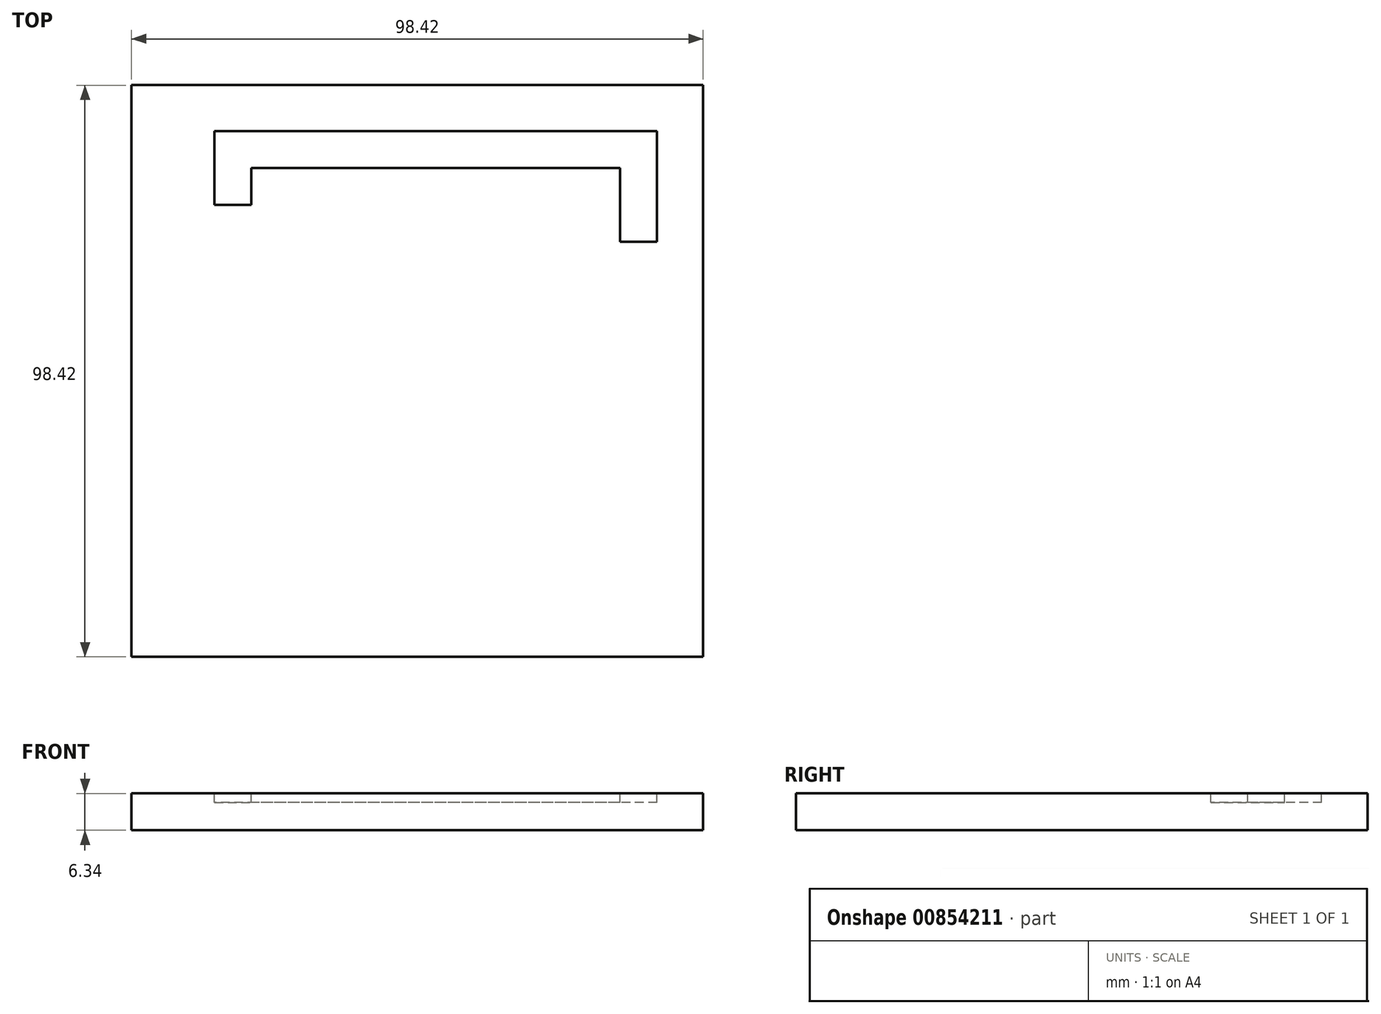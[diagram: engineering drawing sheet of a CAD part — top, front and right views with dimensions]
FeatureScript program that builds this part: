
annotation { "Feature Type Name" : "Feature", "Feature Type Description" : "" }
export const myFeature = defineFeature(function(context is Context, id is Id, definition is map)
    precondition{}
    {
        {
            var Q0;
            Q0=qCreatedBy(makeId("Top.planeOp"),FACE);
            var sketch = newSketch(context, id + "F0", { "sketchPlane" : qUnion([Q0])});
            skLineSegment(sketch, "E0.bottom", {"start": v(49.21, -49.21) * mm, "end": v(-49.21, -49.21) * mm});
            skLineSegment(sketch, "E0.top", {"start": v(49.21, 49.21) * mm, "end": v(-49.21, 49.21) * mm});
            skLineSegment(sketch, "E0.left", {"start": v(49.21, -49.21) * mm, "end": v(49.21, 49.21) * mm});
            skLineSegment(sketch, "E0.right", {"start": v(-49.21, -49.21) * mm, "end": v(-49.21, 49.21) * mm});
            skPoint(sketch, "E0.middle", {"position": v(0, 0) * mm});
            skSolve(sketch);
        }
        {
            var Q0;
            Q0 = qSketchRegion(id + "F0", true);
            extrude(context, id + "F1", {"entities" : qUnion([Q0]), "endBound" : BoundingType.SYMMETRIC, "depth" : 6.35 * mm, "offsetDistance" : 25.4 * mm});
        }
        {
            var Q0;
            Q0=makeQuery(id+"F1.opExtrude","CAP_FACE",FACE,{"disambiguationData":[OSD([sQuery(id+"F0.wireOp",EDGE,"E0.bottom"),sQuery(id+"F0.wireOp",EDGE,"E0.top"),sQuery(id+"F0.wireOp",EDGE,"E0.left"),sQuery(id+"F0.wireOp",EDGE,"E0.right")])],"isStart":false});
            var sketch = newSketch(context, id + "F2", { "sketchPlane" : qUnion([Q0])});
            skLineSegment(sketch, "E1", {"start": v(41.27, 41.28) * mm, "end": v(-34.93, 41.28) * mm});
            skLineSegment(sketch, "E2", {"start": v(41.27, 41.28) * mm, "end": v(41.28, 22.23) * mm});
            skLineSegment(sketch, "E3", {"start": v(-34.93, 41.28) * mm, "end": v(-34.93, 28.58) * mm});
            skLineSegment(sketch, "E4", {"start": v(41.28, 22.23) * mm, "end": v(34.92, 22.23) * mm});
            skLineSegment(sketch, "E5", {"start": v(-34.93, 28.58) * mm, "end": v(-28.58, 28.58) * mm});
            skLineSegment(sketch, "E6", {"start": v(34.93, 22.23) * mm, "end": v(34.92, 34.93) * mm});
            skLineSegment(sketch, "E7", {"start": v(34.92, 34.93) * mm, "end": v(-28.58, 34.93) * mm});
            skLineSegment(sketch, "E8", {"start": v(-28.58, 34.93) * mm, "end": v(-28.58, 28.58) * mm});
            skSolve(sketch);
        }
        {
            var Q0;
            Q0 = qSketchRegion(id + "F2", true);
            extrude(context, id + "F3", {"entities" : qUnion([Q0]), "operationType" : NewBodyOperationType.REMOVE, "endBound" : BoundingType.SYMMETRIC, "oppositeDirection" : true, "depth" : 3.17 * mm, "offsetDistance" : 25.4 * mm});
        }
    });
